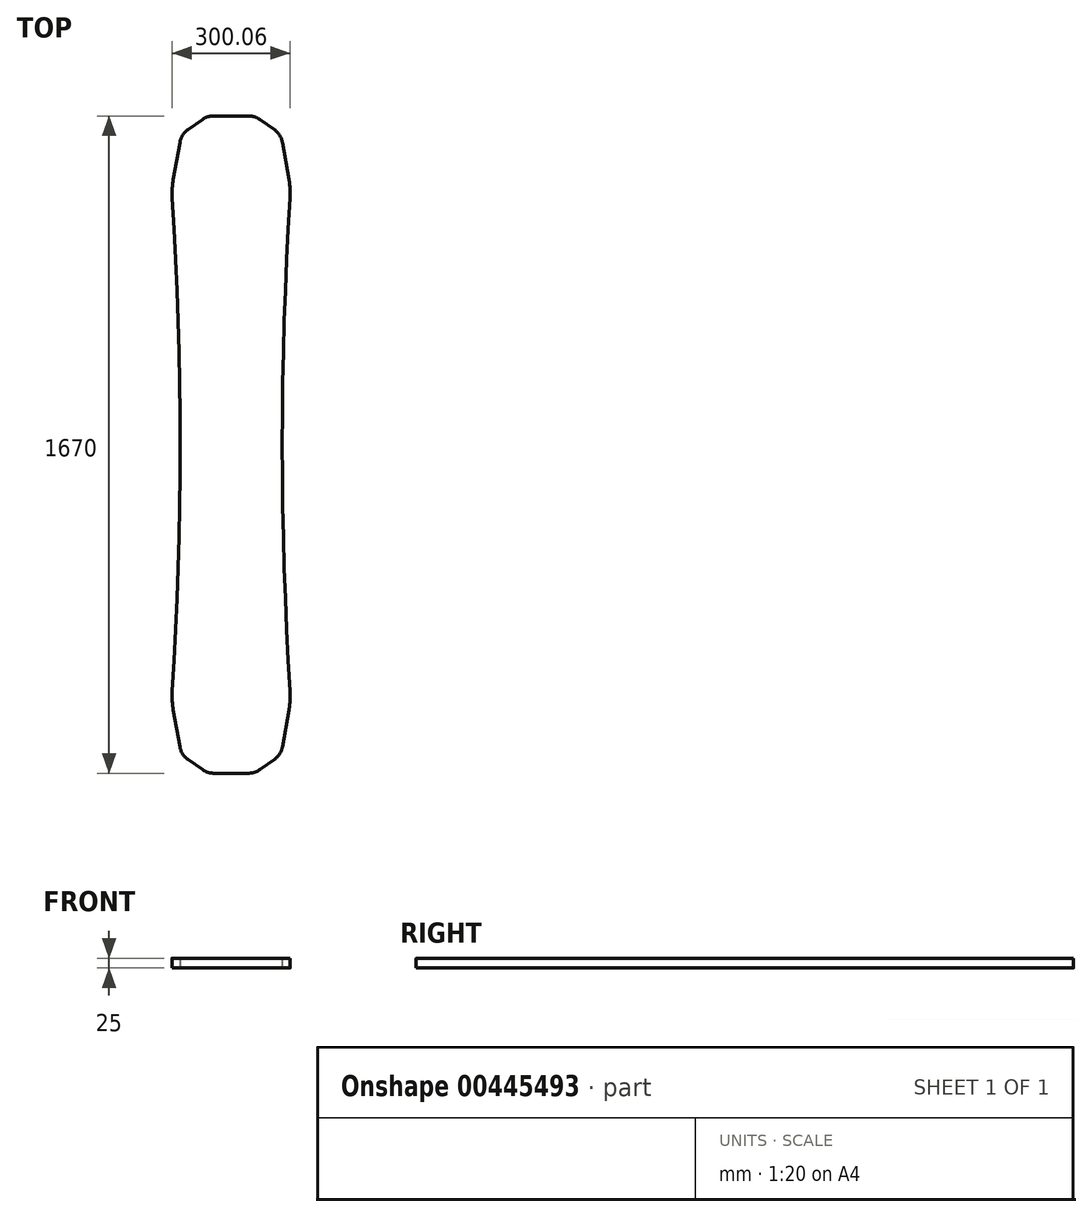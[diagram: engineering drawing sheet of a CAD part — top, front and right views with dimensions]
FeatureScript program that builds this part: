
annotation { "Feature Type Name" : "Feature", "Feature Type Description" : "" }
export const myFeature = defineFeature(function(context is Context, id is Id, definition is map)
    precondition{}
    {
        {
            var Q0;
            Q0=qCreatedBy(makeId("Top.planeOp"),FACE);
            var sketch = newSketch(context, id + "F0", { "sketchPlane" : qUnion([Q0])});
            skLineSegment(sketch, "E0", {"start": v(0, 0) * mm, "end": v(0, 850) * mm, "construction": true});
            skLineSegment(sketch, "E1", {"start": v(130, 0) * mm, "end": v(130, 850) * mm, "construction": true});
            skLineSegment(sketch, "E2.MirrorCS", {"start": v(-130, 0) * mm, "end": v(-130, 850) * mm, "construction": true});
            skLineSegment(sketch, "E3", {"start": v(-130, 0) * mm, "end": v(130, 0) * mm, "construction": true});
            skLineSegment(sketch, "E4", {"start": v(-130, 835) * mm, "end": v(130, 835) * mm, "construction": true});
            skArc(sketch, "E5", {"start": v(-130, 0) * mm, "mid": v(-134.9, 313.32) * mm, "end": v(-149.63, 626.33) * mm});
            skArc(sketch, "E6.MirrorC", {"start": v(130, 0) * mm, "mid": v(134.9, 313.32) * mm, "end": v(149.63, 626.33) * mm});
            skPoint(sketch, "E7", {"position": v(-151.15, 650) * mm});
            skLineSegment(sketch, "E8", {"start": v(-151.15, 650) * mm, "end": v(151.15, 650) * mm, "construction": true});
            skLineSegment(sketch, "E9", {"start": v(0, 835) * mm, "end": v(-44.24, 835) * mm});
            skLineSegment(sketch, "E10", {"start": v(-72.91, 825.96) * mm, "end": v(-109.8, 800.13) * mm});
            skLineSegment(sketch, "E11", {"start": v(-130.37, 767.85) * mm, "end": v(-146.99, 673.59) * mm});
            skPoint(sketch, "E12.visualSharp", {"position": v(-60, 835) * mm});
            skArc(sketch, "E12.filletArc", {"start": v(-44.24, 835) * mm, "mid": v(-59.27, 832.69) * mm, "end": v(-72.91, 825.96) * mm});
            skPoint(sketch, "E13.visualSharp", {"position": v(-126.77, 788.25) * mm});
            skArc(sketch, "E13.filletArc", {"start": v(-109.8, 800.13) * mm, "mid": v(-123.3, 786.03) * mm, "end": v(-130.37, 767.85) * mm});
            skArc(sketch, "E14.filletArc", {"start": v(-146.99, 673.59) * mm, "mid": v(-149.71, 650.04) * mm, "end": v(-149.63, 626.33) * mm});
            skLineSegment(sketch, "E15.MirrorCS", {"start": v(0, 835) * mm, "end": v(44.24, 835) * mm});
            skArc(sketch, "E16.MirrorCS", {"start": v(44.24, 835) * mm, "mid": v(59.27, 832.69) * mm, "end": v(72.91, 825.96) * mm});
            skLineSegment(sketch, "E17.MirrorCS", {"start": v(72.91, 825.96) * mm, "end": v(109.8, 800.13) * mm});
            skArc(sketch, "E18.MirrorCS", {"start": v(109.8, 800.13) * mm, "mid": v(123.3, 786.03) * mm, "end": v(130.37, 767.85) * mm});
            skLineSegment(sketch, "E19.MirrorCS", {"start": v(130.37, 767.85) * mm, "end": v(146.99, 673.59) * mm});
            skArc(sketch, "E20.MirrorCS", {"start": v(146.99, 673.59) * mm, "mid": v(149.71, 650.04) * mm, "end": v(149.63, 626.33) * mm});
            skArc(sketch, "E21.MirrorCS", {"start": v(130, 0) * mm, "mid": v(134.9, -313.32) * mm, "end": v(149.63, -626.33) * mm});
            skArc(sketch, "E22.MirrorCS", {"start": v(-130, 0) * mm, "mid": v(-134.9, -313.32) * mm, "end": v(-149.63, -626.33) * mm});
            skArc(sketch, "E23.MirrorCS", {"start": v(-146.99, -673.59) * mm, "mid": v(-149.71, -650.04) * mm, "end": v(-149.63, -626.33) * mm});
            skLineSegment(sketch, "E24.MirrorCS", {"start": v(-130.37, -767.85) * mm, "end": v(-146.99, -673.59) * mm});
            skArc(sketch, "E25.MirrorCS", {"start": v(-109.8, -800.13) * mm, "mid": v(-123.3, -786.03) * mm, "end": v(-130.37, -767.85) * mm});
            skLineSegment(sketch, "E26.MirrorCS", {"start": v(-72.91, -825.96) * mm, "end": v(-109.8, -800.13) * mm});
            skArc(sketch, "E27.MirrorCS", {"start": v(-44.24, -835) * mm, "mid": v(-59.27, -832.69) * mm, "end": v(-72.91, -825.96) * mm});
            skLineSegment(sketch, "E28.MirrorCS", {"start": v(0, -835) * mm, "end": v(-44.24, -835) * mm});
            skLineSegment(sketch, "E29.MirrorCS", {"start": v(0, -835) * mm, "end": v(44.24, -835) * mm});
            skArc(sketch, "E30.MirrorCS", {"start": v(44.24, -835) * mm, "mid": v(59.27, -832.69) * mm, "end": v(72.91, -825.96) * mm});
            skLineSegment(sketch, "E31.MirrorCS", {"start": v(72.91, -825.96) * mm, "end": v(109.8, -800.13) * mm});
            skArc(sketch, "E32.MirrorCS", {"start": v(109.8, -800.13) * mm, "mid": v(123.3, -786.03) * mm, "end": v(130.37, -767.85) * mm});
            skLineSegment(sketch, "E33.MirrorCS", {"start": v(130.37, -767.85) * mm, "end": v(146.99, -673.59) * mm});
            skArc(sketch, "E34.MirrorCS", {"start": v(146.99, -673.59) * mm, "mid": v(149.71, -650.04) * mm, "end": v(149.63, -626.33) * mm});
            skSolve(sketch);
        }
        {
            var Q0;
            Q0 = qSketchRegion(id + "F0", true);
            extrude(context, id + "F1", {"entities" : qUnion([Q0]), "depth" : 25 * mm});
        }
    });
